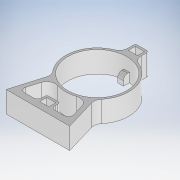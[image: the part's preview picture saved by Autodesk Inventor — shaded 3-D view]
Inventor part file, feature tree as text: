
AUTODESK INVENTOR PART (.ipt)
format: ipt  version: 2018.2 (Build 222227000, 227)  size: 231,424 bytes
history: native  units: mm
features: extrude x2, fillet x2, sketch x1
ambient origin geometry x8: Origin, YZ Plane, XZ Plane, XY Plane, X Axis, Y Axis, Z Axis, Center Point
bodies: Solid1 (feature_tree)
feature tree (5):
  sketch  "Sketch1"  dims[d0=27.84mm d1=1.0mm d2=3.0mm d3=2.0mm d4=2.0mm d5=28.0mm d6=30.0mm d7=20.0mm d8=10.0mm d9=0.0mm d10=3.0mm d11=4.0mm d12=3.0mm d13=0.3mm d14=0.15mm d15=0.15mm d16=1.0mm d17=1.0mm d18=1.0mm d19=4.0mm d20=2.0mm d21=1.0mm d22=2.96mm d23=2.96mm d24=0.15mm d25=0.15mm d26=0.15mm d27=4.3mm d28=0.0mm d29=2.0mm d30=3.0mm d31=4.0mm d32=17.0mm d33=0.15mm d34=1.0mm d35=1.0mm d36=1.0mm]
  extrude  "Extrusion1"  Depth=1.0mm
  fillet  "Fillet1"  Radius=3.0mm
  extrude  "Extrusion2"  Depth=2.0mm
  fillet  "Fillet2"  Radius=2.0mm
